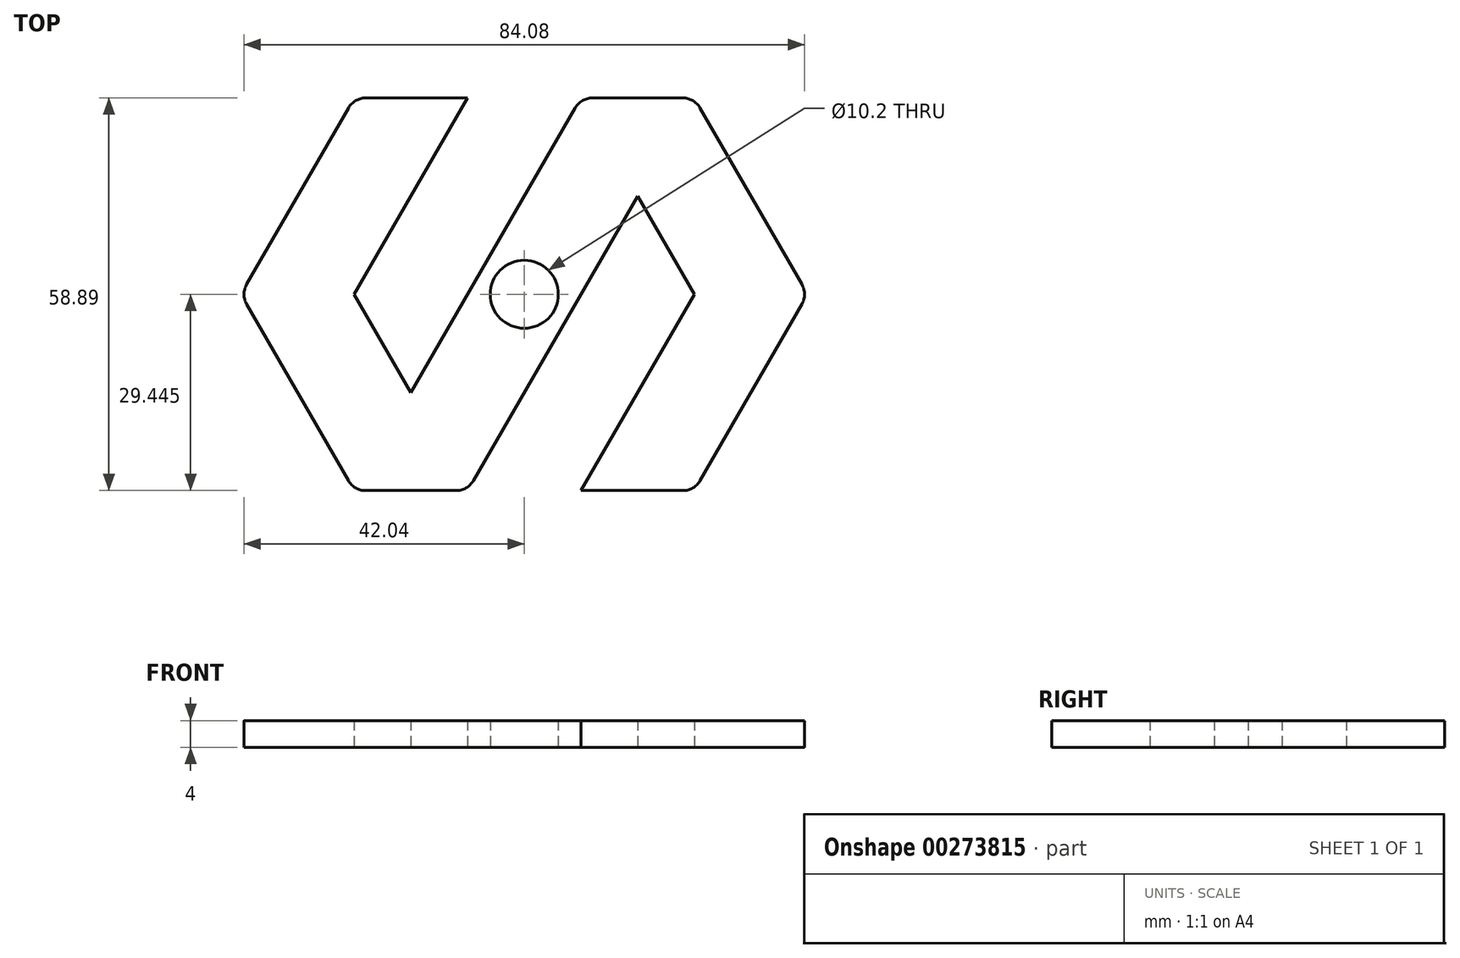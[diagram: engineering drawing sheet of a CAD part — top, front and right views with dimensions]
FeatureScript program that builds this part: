
annotation { "Feature Type Name" : "Feature", "Feature Type Description" : "" }
export const myFeature = defineFeature(function(context is Context, id is Id, definition is map)
    precondition{}
    {
        {
            var Q0;
            Q0=qCreatedBy(makeId("Top.planeOp"),FACE);
            var sketch = newSketch(context, id + "F0", { "sketchPlane" : qUnion([Q0])});
            skLineSegment(sketch, "E0", {"start": v(0, 0) * mm, "end": v(17, 0) * mm});
            skLineSegment(sketch, "E1", {"start": v(17, 0) * mm, "end": v(25.5, 14.72) * mm});
            skLineSegment(sketch, "E2", {"start": v(25.5, 14.72) * mm, "end": v(34, 29.44) * mm});
            skLineSegment(sketch, "E3", {"start": v(34, 29.44) * mm, "end": v(25.5, 44.17) * mm});
            skLineSegment(sketch, "E4", {"start": v(0, 0) * mm, "end": v(8.5, 14.72) * mm});
            skLineSegment(sketch, "E5", {"start": v(8.5, 14.72) * mm, "end": v(17, 29.44) * mm});
            skLineSegment(sketch, "E6", {"start": v(17, 29.44) * mm, "end": v(8.5, 44.17) * mm});
            skLineSegment(sketch, "E7", {"start": v(25.5, 44.17) * mm, "end": v(17, 58.89) * mm});
            skLineSegment(sketch, "E8", {"start": v(8.5, 44.17) * mm, "end": v(0, 29.44) * mm});
            skLineSegment(sketch, "E9", {"start": v(0, 29.44) * mm, "end": v(-8.5, 14.72) * mm});
            skLineSegment(sketch, "E10", {"start": v(-8.5, 14.72) * mm, "end": v(-17, 0) * mm});
            skLineSegment(sketch, "E11", {"start": v(-17, 0) * mm, "end": v(-34, 0) * mm});
            skLineSegment(sketch, "E12", {"start": v(-34, 0) * mm, "end": v(-42.5, 14.72) * mm});
            skLineSegment(sketch, "E13", {"start": v(-42.5, 14.72) * mm, "end": v(-51, 29.44) * mm});
            skLineSegment(sketch, "E14", {"start": v(-51, 29.44) * mm, "end": v(-42.5, 44.17) * mm});
            skLineSegment(sketch, "E15", {"start": v(-42.5, 44.17) * mm, "end": v(-34, 58.89) * mm});
            skLineSegment(sketch, "E16", {"start": v(-34, 58.89) * mm, "end": v(-17, 58.89) * mm});
            skLineSegment(sketch, "E17", {"start": v(17, 58.89) * mm, "end": v(0, 58.89) * mm});
            skLineSegment(sketch, "E18", {"start": v(-17, 58.89) * mm, "end": v(-25.5, 44.17) * mm});
            skLineSegment(sketch, "E19", {"start": v(-25.5, 44.17) * mm, "end": v(-34, 29.44) * mm});
            skLineSegment(sketch, "E20", {"start": v(-34, 29.44) * mm, "end": v(-25.5, 14.72) * mm});
            skLineSegment(sketch, "E21", {"start": v(-25.5, 14.72) * mm, "end": v(-17, 29.44) * mm});
            skLineSegment(sketch, "E22", {"start": v(-17, 29.44) * mm, "end": v(-8.5, 44.17) * mm});
            skLineSegment(sketch, "E23", {"start": v(-8.5, 44.17) * mm, "end": v(0, 58.89) * mm});
            skLineSegment(sketch, "E24", {"start": v(-17, 29.44) * mm, "end": v(0, 29.44) * mm, "construction": true});
            skLineSegment(sketch, "E25", {"start": v(-8.5, 44.17) * mm, "end": v(-8.5, 14.72) * mm, "construction": true});
            skPoint(sketch, "E26", {"position": v(-8.5, 29.44) * mm});
            skLineSegment(sketch, "E27", {"start": v(8.5, 14.72) * mm, "end": v(17, 0) * mm, "construction": true});
            skLineSegment(sketch, "E28", {"start": v(0, 0) * mm, "end": v(25.5, 14.72) * mm, "construction": true});
            skLineSegment(sketch, "E29", {"start": v(-42.5, 44.17) * mm, "end": v(-17, 58.89) * mm, "construction": true});
            skLineSegment(sketch, "E30", {"start": v(-34, 58.89) * mm, "end": v(-25.5, 44.17) * mm, "construction": true});
            skPoint(sketch, "E31", {"position": v(-29.75, 51.53) * mm});
            skPoint(sketch, "E32", {"position": v(12.75, 7.36) * mm});
            skLineSegment(sketch, "E33", {"start": v(-51, 29.44) * mm, "end": v(-34, 29.44) * mm, "construction": true});
            skLineSegment(sketch, "E34", {"start": v(17, 29.44) * mm, "end": v(34, 29.44) * mm, "construction": true});
            skPoint(sketch, "E35", {"position": v(-42.5, 29.44) * mm});
            skPoint(sketch, "E36", {"position": v(25.5, 29.44) * mm});
            skLineSegment(sketch, "E37", {"start": v(-25.5, 14.72) * mm, "end": v(-25.5, 0) * mm, "construction": true});
            skLineSegment(sketch, "E38", {"start": v(8.5, 44.17) * mm, "end": v(8.5, 58.89) * mm, "construction": true});
            skPoint(sketch, "E39", {"position": v(-25.5, 7.36) * mm});
            skPoint(sketch, "E40", {"position": v(8.5, 51.53) * mm});
            skCircle(sketch, "E41", {"center": v(-8.5, 29.44) * mm, "radius": 5 * mm, "construction": true});
            skSolve(sketch);
        }
        {
            var Q0;
            Q0=qCreatedBy(makeId("Top.planeOp"),FACE);
            var sketch = newSketch(context, id + "F1", { "sketchPlane" : qUnion([Q0])});
            skLineSegment(sketch, "E42", {"start": v(-46.37, 36.14) * mm, "end": v(-38.63, 36.14) * mm});
            skLineSegment(sketch, "E43", {"start": v(-46.37, 22.74) * mm, "end": v(-38.63, 22.74) * mm});
            skLineSegment(sketch, "E44", {"start": v(-46.37, 36.14) * mm, "end": v(-50.24, 29.44) * mm});
            skLineSegment(sketch, "E45", {"start": v(-50.24, 29.44) * mm, "end": v(-46.37, 22.74) * mm});
            skLineSegment(sketch, "E46", {"start": v(-38.63, 22.74) * mm, "end": v(-34.76, 29.44) * mm});
            skLineSegment(sketch, "E47", {"start": v(-34.76, 29.44) * mm, "end": v(-38.63, 36.14) * mm});
            skLineSegment(sketch, "E48", {"start": v(-48.3, 32.8) * mm, "end": v(-36.7, 26.1) * mm, "construction": true});
            skLineSegment(sketch, "E49", {"start": v(-48.3, 26.1) * mm, "end": v(-36.7, 32.8) * mm, "construction": true});
            skLineSegment(sketch, "E50", {"start": v(-42.5, 36.14) * mm, "end": v(-42.5, 22.74) * mm, "construction": true});
            skPoint(sketch, "E51", {"position": v(-42.5, 29.44) * mm});
            skLineSegment(sketch, "E52", {"start": v(21.63, 36.14) * mm, "end": v(29.37, 36.14) * mm});
            skLineSegment(sketch, "E53", {"start": v(21.63, 22.74) * mm, "end": v(29.37, 22.74) * mm});
            skLineSegment(sketch, "E54", {"start": v(21.63, 36.14) * mm, "end": v(17.76, 29.44) * mm});
            skLineSegment(sketch, "E55", {"start": v(17.76, 29.44) * mm, "end": v(21.63, 22.74) * mm});
            skLineSegment(sketch, "E56", {"start": v(29.37, 22.74) * mm, "end": v(33.24, 29.44) * mm});
            skLineSegment(sketch, "E57", {"start": v(33.24, 29.44) * mm, "end": v(29.37, 36.14) * mm});
            skLineSegment(sketch, "E58", {"start": v(19.7, 32.8) * mm, "end": v(31.3, 26.1) * mm, "construction": true});
            skLineSegment(sketch, "E59", {"start": v(19.7, 26.1) * mm, "end": v(31.3, 32.8) * mm, "construction": true});
            skLineSegment(sketch, "E60", {"start": v(25.5, 36.14) * mm, "end": v(25.5, 22.74) * mm, "construction": true});
            skPoint(sketch, "E61", {"position": v(25.5, 29.44) * mm});
            skLineSegment(sketch, "E62", {"start": v(-29.37, 14.06) * mm, "end": v(-21.63, 14.06) * mm});
            skLineSegment(sketch, "E63", {"start": v(-29.37, 0.66) * mm, "end": v(-21.63, 0.66) * mm});
            skLineSegment(sketch, "E64", {"start": v(-29.37, 14.06) * mm, "end": v(-33.24, 7.36) * mm});
            skLineSegment(sketch, "E65", {"start": v(-33.24, 7.36) * mm, "end": v(-29.37, 0.66) * mm});
            skLineSegment(sketch, "E66", {"start": v(-21.63, 0.66) * mm, "end": v(-17.76, 7.36) * mm});
            skLineSegment(sketch, "E67", {"start": v(-17.76, 7.36) * mm, "end": v(-21.63, 14.06) * mm});
            skLineSegment(sketch, "E68", {"start": v(-31.3, 10.71) * mm, "end": v(-19.7, 4.01) * mm, "construction": true});
            skLineSegment(sketch, "E69", {"start": v(-31.3, 4.01) * mm, "end": v(-19.7, 10.71) * mm, "construction": true});
            skLineSegment(sketch, "E70", {"start": v(-25.5, 14.06) * mm, "end": v(-25.5, 0.66) * mm, "construction": true});
            skPoint(sketch, "E71", {"position": v(-25.5, 7.36) * mm});
            skLineSegment(sketch, "E72", {"start": v(-33.62, 58.23) * mm, "end": v(-25.88, 58.23) * mm});
            skLineSegment(sketch, "E73", {"start": v(-33.62, 44.83) * mm, "end": v(-25.88, 44.83) * mm});
            skLineSegment(sketch, "E74", {"start": v(-33.62, 58.23) * mm, "end": v(-37.49, 51.53) * mm});
            skLineSegment(sketch, "E75", {"start": v(-37.49, 51.53) * mm, "end": v(-33.62, 44.83) * mm});
            skLineSegment(sketch, "E76", {"start": v(-25.88, 44.83) * mm, "end": v(-22.01, 51.53) * mm});
            skLineSegment(sketch, "E77", {"start": v(-22.01, 51.53) * mm, "end": v(-25.88, 58.23) * mm});
            skLineSegment(sketch, "E78", {"start": v(-35.55, 54.88) * mm, "end": v(-23.95, 48.18) * mm, "construction": true});
            skLineSegment(sketch, "E79", {"start": v(-35.55, 48.18) * mm, "end": v(-23.95, 54.88) * mm, "construction": true});
            skLineSegment(sketch, "E80", {"start": v(-29.75, 58.23) * mm, "end": v(-29.75, 44.83) * mm, "construction": true});
            skPoint(sketch, "E81", {"position": v(-29.75, 51.53) * mm});
            skLineSegment(sketch, "E82", {"start": v(4.63, 58.23) * mm, "end": v(12.37, 58.23) * mm});
            skLineSegment(sketch, "E83", {"start": v(4.63, 44.83) * mm, "end": v(12.37, 44.83) * mm});
            skLineSegment(sketch, "E84", {"start": v(4.63, 58.23) * mm, "end": v(0.76, 51.53) * mm});
            skLineSegment(sketch, "E85", {"start": v(0.76, 51.53) * mm, "end": v(4.63, 44.83) * mm});
            skLineSegment(sketch, "E86", {"start": v(12.37, 44.83) * mm, "end": v(16.24, 51.53) * mm});
            skLineSegment(sketch, "E87", {"start": v(16.24, 51.53) * mm, "end": v(12.37, 58.23) * mm});
            skLineSegment(sketch, "E88", {"start": v(2.7, 54.88) * mm, "end": v(14.3, 48.18) * mm, "construction": true});
            skLineSegment(sketch, "E89", {"start": v(2.7, 48.18) * mm, "end": v(14.3, 54.88) * mm, "construction": true});
            skLineSegment(sketch, "E90", {"start": v(8.5, 58.23) * mm, "end": v(8.5, 44.83) * mm, "construction": true});
            skPoint(sketch, "E91", {"position": v(8.5, 51.53) * mm});
            skLineSegment(sketch, "E92", {"start": v(8.88, 14.06) * mm, "end": v(16.62, 14.06) * mm});
            skLineSegment(sketch, "E93", {"start": v(8.88, 0.66) * mm, "end": v(16.62, 0.66) * mm});
            skLineSegment(sketch, "E94", {"start": v(8.88, 14.06) * mm, "end": v(5.01, 7.36) * mm});
            skLineSegment(sketch, "E95", {"start": v(5.01, 7.36) * mm, "end": v(8.88, 0.66) * mm});
            skLineSegment(sketch, "E96", {"start": v(16.62, 0.66) * mm, "end": v(20.49, 7.36) * mm});
            skLineSegment(sketch, "E97", {"start": v(20.49, 7.36) * mm, "end": v(16.62, 14.06) * mm});
            skLineSegment(sketch, "E98", {"start": v(6.95, 10.71) * mm, "end": v(18.55, 4.01) * mm, "construction": true});
            skLineSegment(sketch, "E99", {"start": v(6.95, 4.01) * mm, "end": v(18.55, 10.71) * mm, "construction": true});
            skLineSegment(sketch, "E100", {"start": v(12.75, 14.06) * mm, "end": v(12.75, 0.66) * mm, "construction": true});
            skPoint(sketch, "E101", {"position": v(12.75, 7.36) * mm});
            skSolve(sketch);
        }
        {
            var Q0;
            Q0=makeQuery(id+"F0.imprint","IMPRINT",FACE,{"disambiguationData":[TD([[makeQuery(id+"F0.imprint","IMPRINT",EDGE,{"derivedFrom":sQuery(id+"F0.wireOp",EDGE,"E0")}),1.0]])]});
            extrude(context, id + "F2", {"entities" : qUnion([Q0]), "depth" : 4 * mm});
        }
        {
            var Q0;
            Q0=sQuery(id+"F0.wireOp",VERTEX,"E26");
            var Q1;
            Q1=makeQuery(id+"F2.opExtrude","SWEPT_BODY",BODY,{"disambiguationData":[OSD([sQuery(id+"F0.wireOp",EDGE,"E0"),sQuery(id+"F0.wireOp",EDGE,"E1"),sQuery(id+"F0.wireOp",EDGE,"E2"),sQuery(id+"F0.wireOp",EDGE,"E3"),sQuery(id+"F0.wireOp",EDGE,"E4"),sQuery(id+"F0.wireOp",EDGE,"E5"),sQuery(id+"F0.wireOp",EDGE,"E6"),sQuery(id+"F0.wireOp",EDGE,"E7"),sQuery(id+"F0.wireOp",EDGE,"E8"),sQuery(id+"F0.wireOp",EDGE,"E9"),sQuery(id+"F0.wireOp",EDGE,"E10"),sQuery(id+"F0.wireOp",EDGE,"E11"),sQuery(id+"F0.wireOp",EDGE,"E12"),sQuery(id+"F0.wireOp",EDGE,"E13"),sQuery(id+"F0.wireOp",EDGE,"E14"),sQuery(id+"F0.wireOp",EDGE,"E15"),sQuery(id+"F0.wireOp",EDGE,"E16"),sQuery(id+"F0.wireOp",EDGE,"E17"),sQuery(id+"F0.wireOp",EDGE,"E18"),sQuery(id+"F0.wireOp",EDGE,"E19"),sQuery(id+"F0.wireOp",EDGE,"E20"),sQuery(id+"F0.wireOp",EDGE,"E21"),sQuery(id+"F0.wireOp",EDGE,"E22"),sQuery(id+"F0.wireOp",EDGE,"E23")])]});
            hole(context, id + "F3", {"style" : HoleStyle.SIMPLE, "endStyle" : HoleEndStyle.THROUGH, "oppositeDirection" : true, "holeDiameter" : 10.2 * mm, "tappedDepth" : 12 * mm, "tapClearance" : 3, "locations" : qUnion([Q0]), "scope" : qUnion([Q1])});
        }
        {
            var Q0;
            Q0=makeQuery(id+"F2.opExtrude","SWEPT_EDGE",EDGE,{"disambiguationData":[OSD([sQuery(id+"F0.wireOp",EDGE,"E13"),sQuery(id+"F0.wireOp",EDGE,"E14")])]});
            var Q1;
            Q1=makeQuery(id+"F2.opExtrude","SWEPT_EDGE",EDGE,{"disambiguationData":[OSD([sQuery(id+"F0.wireOp",EDGE,"E15"),sQuery(id+"F0.wireOp",EDGE,"E16")])]});
            var Q2;
            Q2=makeQuery(id+"F2.opExtrude","SWEPT_EDGE",EDGE,{"disambiguationData":[OSD([sQuery(id+"F0.wireOp",EDGE,"E17"),sQuery(id+"F0.wireOp",EDGE,"E23")])]});
            var Q3;
            Q3=makeQuery(id+"F2.opExtrude","SWEPT_EDGE",EDGE,{"disambiguationData":[OSD([sQuery(id+"F0.wireOp",EDGE,"E7"),sQuery(id+"F0.wireOp",EDGE,"E17")])]});
            var Q4;
            Q4=makeQuery(id+"F2.opExtrude","SWEPT_EDGE",EDGE,{"disambiguationData":[OSD([sQuery(id+"F0.wireOp",EDGE,"E2"),sQuery(id+"F0.wireOp",EDGE,"E3")])]});
            var Q5;
            Q5=makeQuery(id+"F2.opExtrude","SWEPT_EDGE",EDGE,{"disambiguationData":[OSD([sQuery(id+"F0.wireOp",EDGE,"E0"),sQuery(id+"F0.wireOp",EDGE,"E1")])]});
            var Q6;
            Q6=makeQuery(id+"F2.opExtrude","SWEPT_EDGE",EDGE,{"disambiguationData":[OSD([sQuery(id+"F0.wireOp",EDGE,"E10"),sQuery(id+"F0.wireOp",EDGE,"E11")])]});
            var Q7;
            Q7=makeQuery(id+"F2.opExtrude","SWEPT_EDGE",EDGE,{"disambiguationData":[OSD([sQuery(id+"F0.wireOp",EDGE,"E11"),sQuery(id+"F0.wireOp",EDGE,"E12")])]});
            fillet(context, id + "F4", {"entities" : qUnion([Q0, Q1, Q2, Q3, Q4, Q5, Q6, Q7]), "radius" : 3 * mm, "tangentPropagation" : true, "allowEdgeOverflow" : false});
        }
    });
